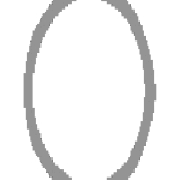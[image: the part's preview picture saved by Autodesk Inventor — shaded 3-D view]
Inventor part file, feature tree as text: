
AUTODESK INVENTOR PART (.ipt)
format: ipt  version: 2021 (Build 250183000, 183)  size: 112,128 bytes
history: native  units: in
note: dims shown in document units (in); Inventor stores cm internally (conversion verified against a paired STEP export)
features: other x4, sketch x3, plane x1
ambient origin geometry x8: Origin, YZ Plane, XZ Plane, XY Plane, X Axis, Y Axis, Z Axis, Center Point
bodies: Solid1 (feature_tree), Body (feature_tree)
feature tree (8):
  other  "Driven Length"
  other  "Frame Generator"
  other  "Start Plane"
  other  "End Plane"
  sketch  "Sketch"  dims[d2=32.7942in d4=-0.0in d5=32.7942in d6=0.12in d7=0.0in d8=90.0deg d9=32.7942in]
  sketch  "Sketch2"  dims[d0=1.0in]
  plane  "Work Plane3"
  sketch  "Sketch3"  dims[d1=0.065in]
